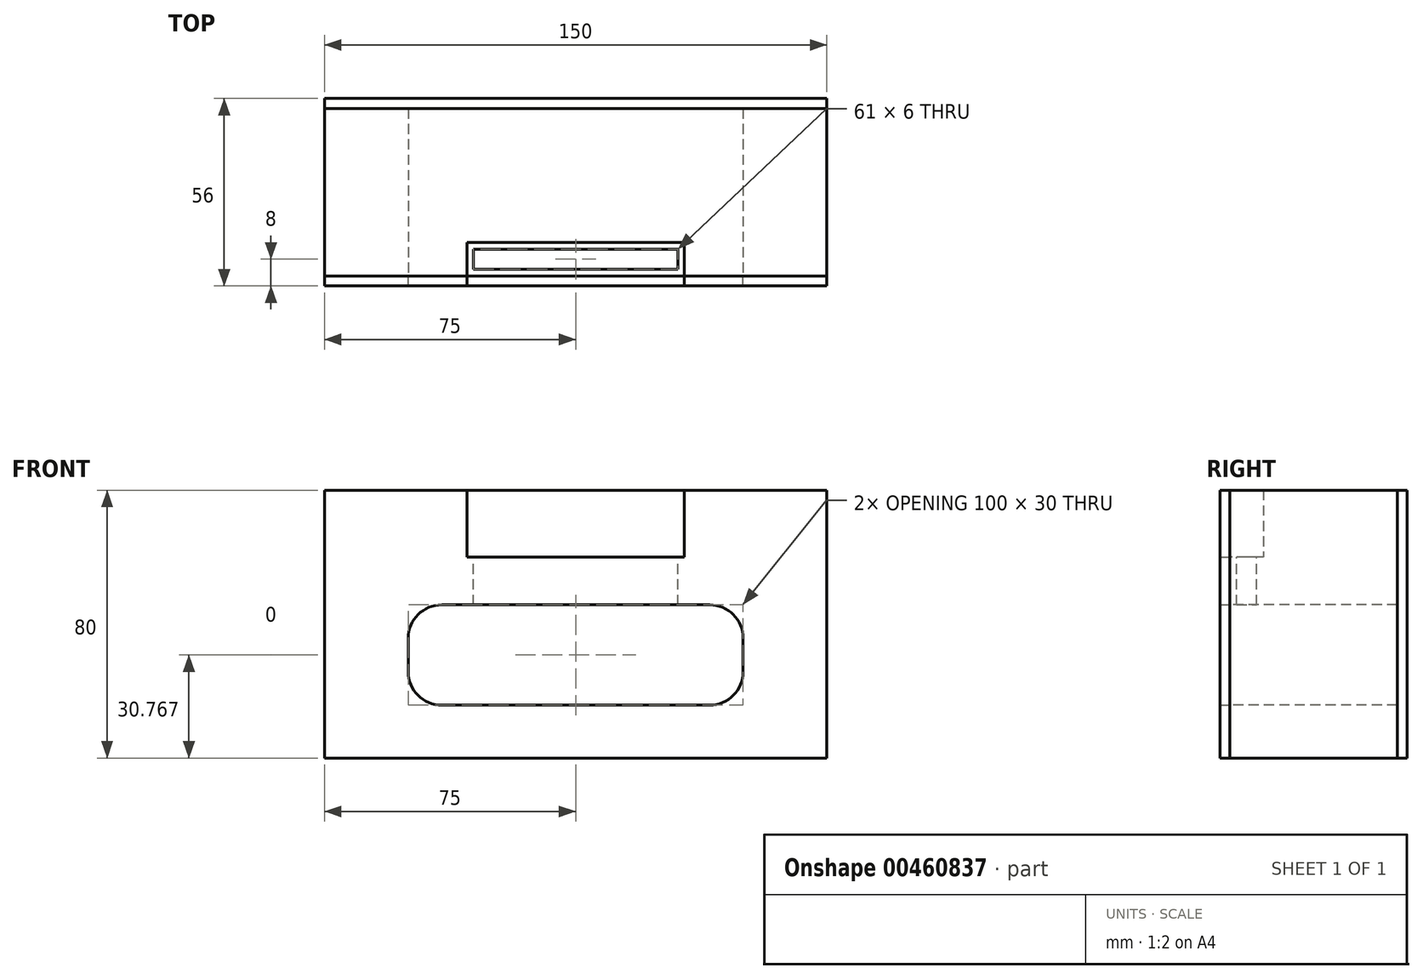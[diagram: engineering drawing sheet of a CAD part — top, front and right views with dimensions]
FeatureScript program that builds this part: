
annotation { "Feature Type Name" : "Feature", "Feature Type Description" : "" }
export const myFeature = defineFeature(function(context is Context, id is Id, definition is map)
    precondition{}
    {
        {
            var Q0;
            Q0=qCreatedBy(makeId("Top.planeOp"),FACE);
            var sketch = newSketch(context, id + "F0", { "sketchPlane" : qUnion([Q0])});
            skLineSegment(sketch, "E0.bottom", {"start": v(75, -25) * mm, "end": v(-75, -25) * mm});
            skLineSegment(sketch, "E0.top", {"start": v(75, 25) * mm, "end": v(-75, 25) * mm});
            skLineSegment(sketch, "E0.left", {"start": v(75, -25) * mm, "end": v(75, 25) * mm});
            skLineSegment(sketch, "E0.right", {"start": v(-75, -25) * mm, "end": v(-75, 25) * mm});
            skPoint(sketch, "E0.middle", {"position": v(0, 0) * mm});
            skSolve(sketch);
        }
        {
            var Q0;
            Q0=makeQuery(id+"F0.imprint","IMPRINT",FACE,{"disambiguationData":[TD([[makeQuery(id+"F0.imprint","IMPRINT",EDGE,{"derivedFrom":sQuery(id+"F0.wireOp",EDGE,"E0.bottom")}),-1.0]])]});
            extrude(context, id + "F1", {"entities" : qUnion([Q0]), "depth" : 80 * mm});
        }
        {
            var Q0;
            Q0=makeQuery(id+"F1.opExtrude","SWEPT_FACE",FACE,{"disambiguationData":[OSD([sQuery(id+"F0.wireOp",EDGE,"E0.bottom")])]});
            var sketch = newSketch(context, id + "F2", { "sketchPlane" : qUnion([Q0])});
            skLineSegment(sketch, "E1.bottom", {"start": v(-32.5, 80) * mm, "end": v(32.5, 80) * mm});
            skLineSegment(sketch, "E1.top", {"start": v(-32.5, 60) * mm, "end": v(32.5, 60) * mm});
            skLineSegment(sketch, "E1.left", {"start": v(-32.5, 80) * mm, "end": v(-32.5, 60) * mm});
            skLineSegment(sketch, "E1.right", {"start": v(32.5, 80) * mm, "end": v(32.5, 60) * mm});
            skSolve(sketch);
        }
        {
            var Q0;
            Q0=makeQuery(id+"F2.imprint","IMPRINT",FACE,{"disambiguationData":[TD([[makeQuery(id+"F2.imprint","IMPRINT",EDGE,{"derivedFrom":sQuery(id+"F2.wireOp",EDGE,"E1.bottom")}),1.0]])]});
            extrude(context, id + "F3", {"entities" : qUnion([Q0]), "operationType" : NewBodyOperationType.REMOVE, "oppositeDirection" : true, "depth" : 10 * mm});
        }
        {
            var Q0;
            Q0=makeQuery(id+"F1.opExtrude","SWEPT_FACE",FACE,{"disambiguationData":[OSD([sQuery(id+"F0.wireOp",EDGE,"E0.bottom")])]});
            var sketch = newSketch(context, id + "F4", { "sketchPlane" : qUnion([Q0])});
            skLineSegment(sketch, "E2.bottom", {"start": v(-40, 45.77) * mm, "end": v(40, 45.77) * mm});
            skLineSegment(sketch, "E2.top", {"start": v(-40, 15.77) * mm, "end": v(40, 15.77) * mm});
            skLineSegment(sketch, "E2.left", {"start": v(-50, 35.77) * mm, "end": v(-50, 25.77) * mm});
            skLineSegment(sketch, "E2.right", {"start": v(50, 35.77) * mm, "end": v(50, 25.77) * mm});
            skPoint(sketch, "E3.visualSharp", {"position": v(-50, 45.77) * mm});
            skArc(sketch, "E3.filletArc", {"start": v(-40, 45.77) * mm, "mid": v(-47.07, 42.84) * mm, "end": v(-50, 35.77) * mm});
            skPoint(sketch, "E4.visualSharp", {"position": v(50, 45.77) * mm});
            skArc(sketch, "E4.filletArc", {"start": v(50, 35.77) * mm, "mid": v(47.07, 42.84) * mm, "end": v(40, 45.77) * mm});
            skPoint(sketch, "E5.visualSharp", {"position": v(50, 15.77) * mm});
            skArc(sketch, "E5.filletArc", {"start": v(40, 15.77) * mm, "mid": v(47.07, 18.7) * mm, "end": v(50, 25.77) * mm});
            skPoint(sketch, "E6.visualSharp", {"position": v(-50, 15.77) * mm});
            skArc(sketch, "E6.filletArc", {"start": v(-50, 25.77) * mm, "mid": v(-47.07, 18.7) * mm, "end": v(-40, 15.77) * mm});
            skSolve(sketch);
        }
        {
            var Q0;
            Q0 = qSketchRegion(id + "F4", true);
            extrude(context, id + "F5", {"entities" : qUnion([Q0]), "operationType" : NewBodyOperationType.REMOVE, "oppositeDirection" : true, "depth" : 67.4 * mm});
        }
        {
            var Q0;
            Q0=makeQuery(id+"F3.boolean.opBoolean","COPY",FACE,{"derivedFrom":makeQuery(id+"F3.opExtrude","SWEPT_FACE",FACE,{"disambiguationData":[OSD([sQuery(id+"F2.wireOp",EDGE,"E1.top")])]})});
            var sketch = newSketch(context, id + "F6", { "sketchPlane" : qUnion([Q0])});
            skLineSegment(sketch, "E7.bottom", {"start": v(-30.5, -17) * mm, "end": v(30.5, -17) * mm});
            skLineSegment(sketch, "E7.top", {"start": v(-30.5, -23) * mm, "end": v(30.5, -23) * mm});
            skLineSegment(sketch, "E7.left", {"start": v(-30.5, -17) * mm, "end": v(-30.5, -23) * mm});
            skLineSegment(sketch, "E7.right", {"start": v(30.5, -17) * mm, "end": v(30.5, -23) * mm});
            skSolve(sketch);
        }
        {
            var Q0;
            Q0=makeQuery(id+"F6.imprint","IMPRINT",FACE,{"disambiguationData":[TD([[makeQuery(id+"F6.imprint","IMPRINT",EDGE,{"derivedFrom":sQuery(id+"F6.wireOp",EDGE,"E7.bottom")}),-1.0]])]});
            extrude(context, id + "F7", {"entities" : qUnion([Q0]), "operationType" : NewBodyOperationType.REMOVE, "oppositeDirection" : true, "depth" : 25 * mm});
        }
        {
            var Q0;
            Q0=makeQuery(id+"F1.opExtrude","SWEPT_FACE",FACE,{"disambiguationData":[OSD([sQuery(id+"F0.wireOp",EDGE,"E0.bottom")])]});
            var sketch = newSketch(context, id + "F8", { "sketchPlane" : qUnion([Q0])});
            skLineSegment(sketch, "E8.bottom", {"start": v(-75, 80) * mm, "end": v(75, 80) * mm});
            skLineSegment(sketch, "E8.top", {"start": v(-75, 0) * mm, "end": v(75, 0) * mm});
            skLineSegment(sketch, "E8.left", {"start": v(-75, 80) * mm, "end": v(-75, 0) * mm});
            skLineSegment(sketch, "E8.right", {"start": v(75, 80) * mm, "end": v(75, 0) * mm});
            skLineSegment(sketch, "E9.0", {"start": v(-40, 45.77) * mm, "end": v(40, 45.77) * mm});
            skArc(sketch, "E10.0", {"start": v(-40, 45.77) * mm, "mid": v(-47.07, 42.84) * mm, "end": v(-50, 35.77) * mm});
            skLineSegment(sketch, "E11.0", {"start": v(-50, 35.77) * mm, "end": v(-50, 25.77) * mm});
            skArc(sketch, "E12.0", {"start": v(-50, 25.77) * mm, "mid": v(-47.07, 18.7) * mm, "end": v(-40, 15.77) * mm});
            skLineSegment(sketch, "E13.0", {"start": v(-40, 15.77) * mm, "end": v(40, 15.77) * mm});
            skArc(sketch, "E14.0", {"start": v(40, 15.77) * mm, "mid": v(47.07, 18.7) * mm, "end": v(50, 25.77) * mm});
            skLineSegment(sketch, "E15.0", {"start": v(50, 35.77) * mm, "end": v(50, 25.77) * mm});
            skArc(sketch, "E16.0", {"start": v(50, 35.77) * mm, "mid": v(47.07, 42.84) * mm, "end": v(40, 45.77) * mm});
            skSolve(sketch);
        }
        {
            var Q0;
            Q0=makeQuery(id+"F8.imprint","IMPRINT",FACE,{"disambiguationData":[TD([[makeQuery(id+"F8.imprint","IMPRINT",EDGE,{"derivedFrom":sQuery(id+"F8.wireOp",EDGE,"E8.top")}),-1.0]])]});
            extrude(context, id + "F9", {"entities" : qUnion([Q0]), "depth" : 3 * mm});
        }
        {
            var Q0;
            Q0=makeQuery(id+"F1.opExtrude","SWEPT_FACE",FACE,{"disambiguationData":[OSD([sQuery(id+"F0.wireOp",EDGE,"E0.top")])]});
            var sketch = newSketch(context, id + "F10", { "sketchPlane" : qUnion([Q0])});
            skLineSegment(sketch, "E17.bottom", {"start": v(75, 80) * mm, "end": v(-75, 80) * mm});
            skLineSegment(sketch, "E17.top", {"start": v(75, 0) * mm, "end": v(-75, 0) * mm});
            skLineSegment(sketch, "E17.left", {"start": v(75, 80) * mm, "end": v(75, 0) * mm});
            skLineSegment(sketch, "E17.right", {"start": v(-75, 80) * mm, "end": v(-75, 0) * mm});
            skSolve(sketch);
        }
        {
            var Q0;
            Q0 = qSketchRegion(id + "F10", true);
            extrude(context, id + "F11", {"entities" : qUnion([Q0]), "depth" : 3 * mm});
        }
    });
